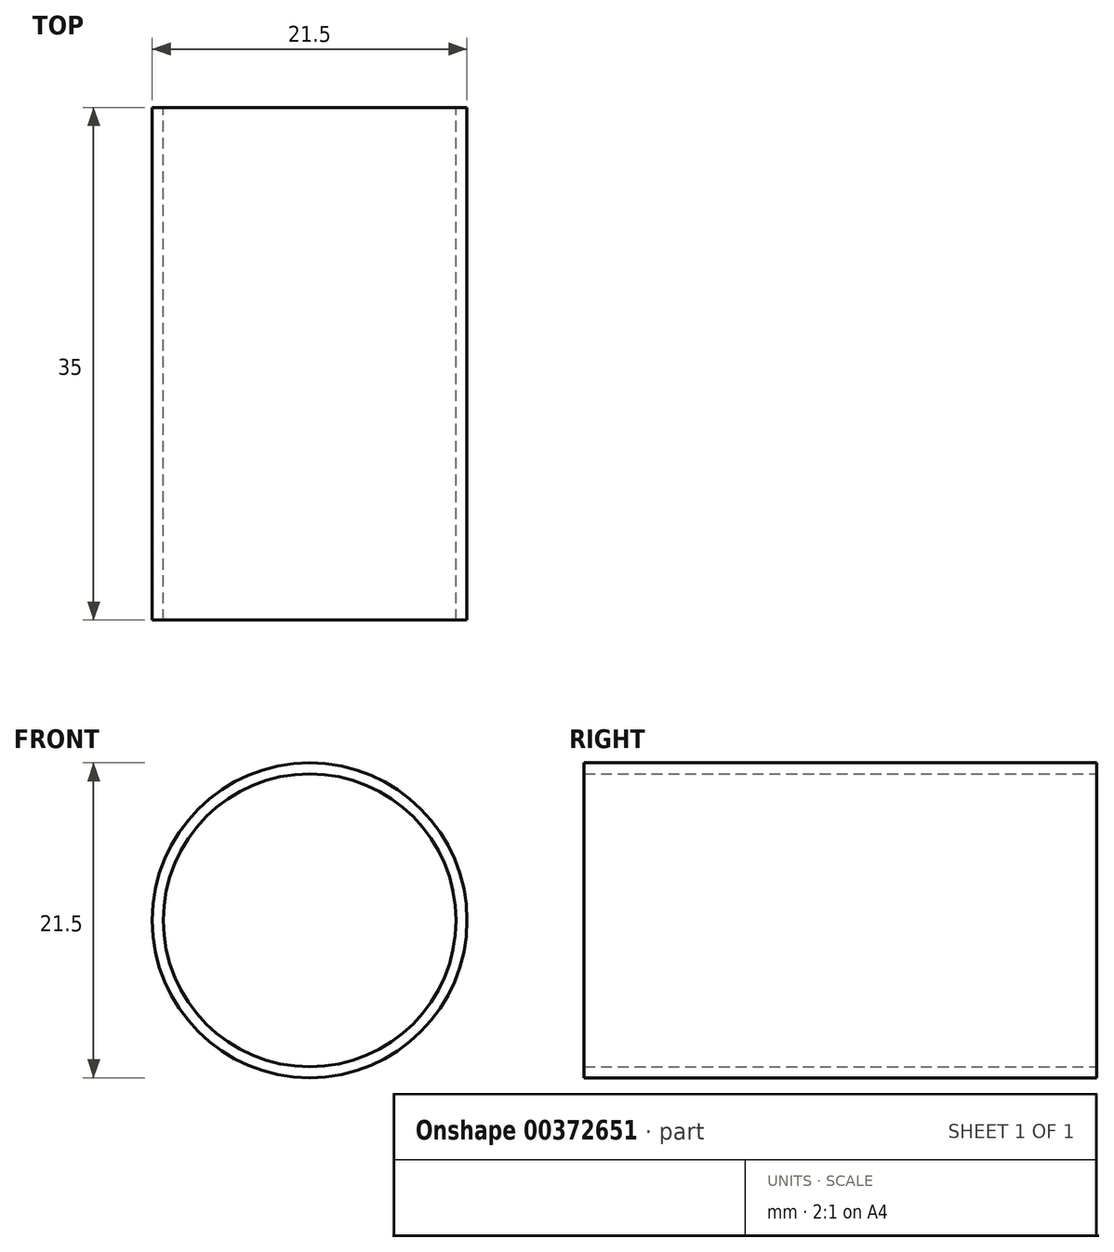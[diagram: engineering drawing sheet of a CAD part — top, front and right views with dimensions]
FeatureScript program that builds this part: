
annotation { "Feature Type Name" : "Feature", "Feature Type Description" : "" }
export const myFeature = defineFeature(function(context is Context, id is Id, definition is map)
    precondition{}
    {
        {
            var Q0;
            Q0=qCreatedBy(makeId("Front.planeOp"), FACE);
            var sketch = newSketch(context, id + "F0", { "sketchPlane" : qUnion([Q0]), "disableImprinting" : false});
            skCircle(sketch, "E0", {"center": v(0, 0) * mm, "radius": 10.75 * mm});
            skCircle(sketch, "E1", {"center": v(0, 0) * mm, "radius": 10 * mm});
            skSolve(sketch);
        }
        {
            var Q0;
            Q0 = qSketchRegion(id + "F0", true);
            extrude(context, id + "F1", {"entities" : qUnion([Q0]), "flatOperationType" : FlatOperationType.REMOVE, "depth" : 35 * mm, "offsetDistance" : 25 * mm, "domain" : OperationDomain.MODEL});
        }
    });
